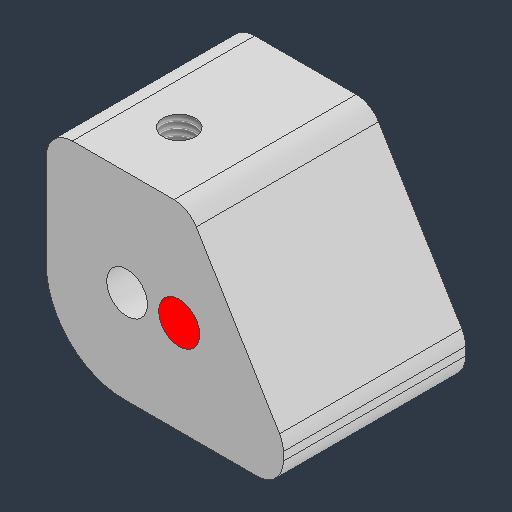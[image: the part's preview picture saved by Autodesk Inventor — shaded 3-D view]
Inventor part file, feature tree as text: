
AUTODESK INVENTOR PART (.ipt)
format: ipt  version: 2024.3 (Build 283343000, 343)  size: 150,016 bytes
history: native  units: in
note: dims shown in document units (in); Inventor stores cm internally (conversion verified against a paired STEP export)
features: sketch x3, hole x3, fillet x2, extrude x1
ambient origin geometry x8: Origin, YZ Plane, XZ Plane, XY Plane, X Axis, Y Axis, Z Axis, Center Point
bodies: Solid1 (feature_tree)
feature tree (9):
  extrude  "Extrusion1"  Depth=0.95in
  sketch  "Sketch2"  dims[d2=0.1875in d3=0.875in d4=0.0in]
  hole  "Hole1"  [1 undecoded]
  hole  "Hole2"  [1 undecoded]
  hole  "Hole3"  [1 undecoded]
  fillet  "Fillet1"  Radius=0.375in
  fillet  "Fillet2"  Radius=0.125in
  sketch  "Sketch1"  dims[d0=0.825in d1=0.95in]
  sketch  "Sketch3"  dims[d5=0.197in d6=0.75in d7=0.217in d8=0.077in d9=90.0deg d10=1.0in d11=0.8108in d12=0.196in d13=0.75in d14=0.385in d15=0.25in d16=0.5635in d17=1.0in d18=0.8108in d19=0.3125in d21=0.3125in d22=0.156in d23=0.38in d24=0.375in d25=0.25in d26=0.5635in d27=0.536in d28=0.8108in d29=0.375in d30=0.125in d31=0.325in]
note: 3 required parameter values undecoded (feature->parameter linkage not recoverable at this tier; creation-order binding heuristic only, values carry confidence <= 0.55)
